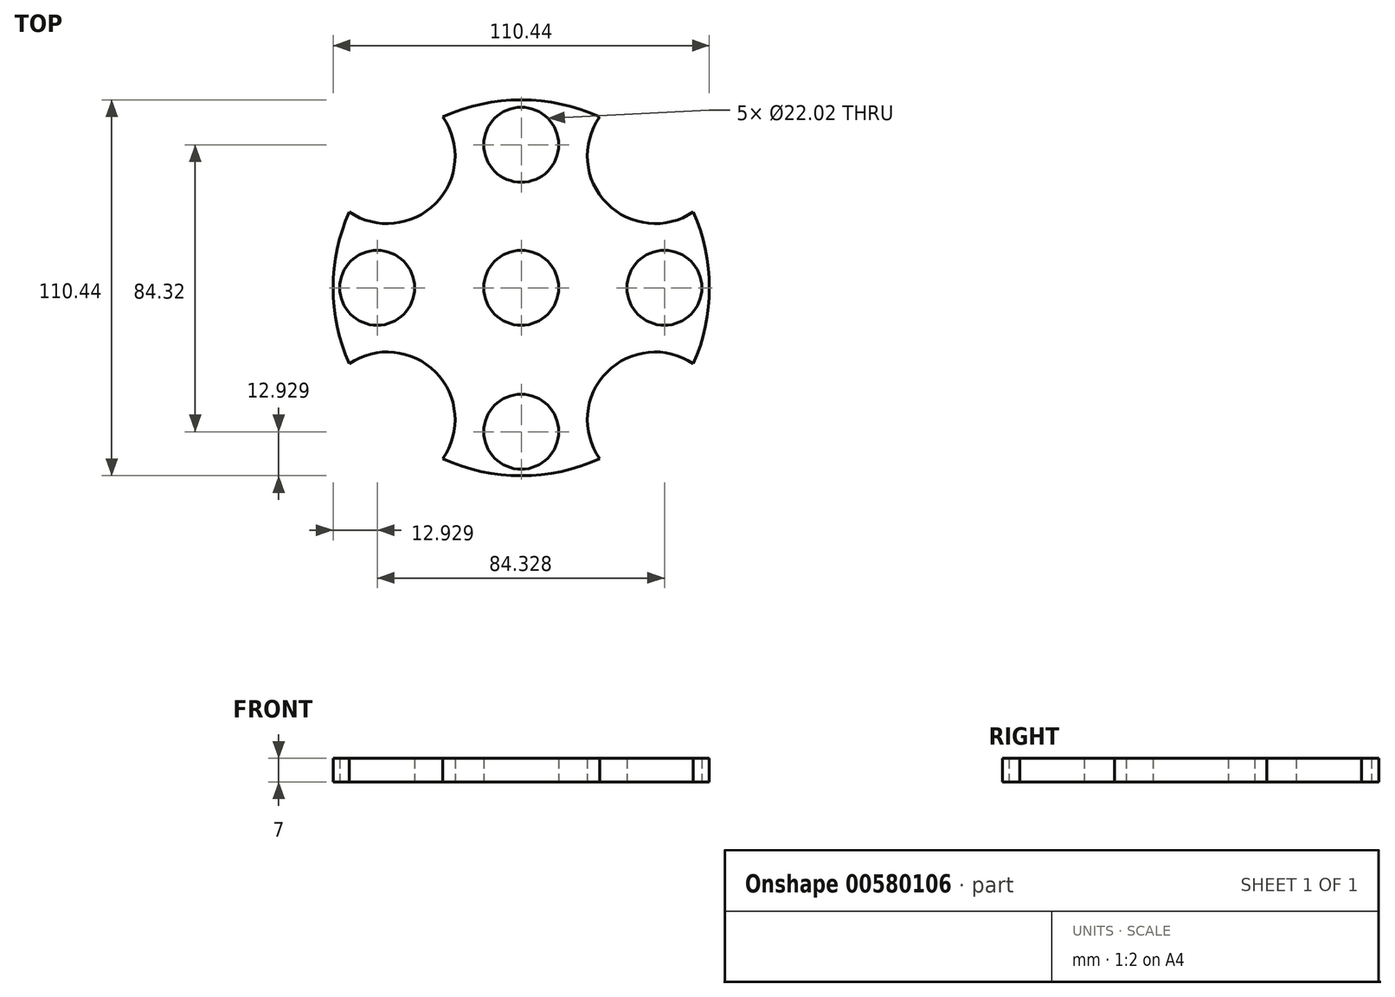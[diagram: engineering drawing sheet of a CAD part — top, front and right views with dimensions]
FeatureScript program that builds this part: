
annotation { "Feature Type Name" : "Feature", "Feature Type Description" : "" }
export const myFeature = defineFeature(function(context is Context, id is Id, definition is map)
    precondition{}
    {
        {
            var Q0;
            Q0=qCreatedBy(makeId("Top.planeOp"),FACE);
            var sketch = newSketch(context, id + "F0", { "sketchPlane" : qUnion([Q0])});
            skCircle(sketch, "E0", {"center": v(0, 0) * mm, "radius": 11.01 * mm});
            skCircle(sketch, "E1", {"center": v(0, 0) * mm, "radius": 55.22 * mm});
            skCircle(sketch, "E2", {"center": v(0, -42.3) * mm, "radius": 11.01 * mm});
            skCircle(sketch, "E3", {"center": v(42.04, 0) * mm, "radius": 11.01 * mm});
            skCircle(sketch, "E4", {"center": v(0, 42.03) * mm, "radius": 11.01 * mm});
            skCircle(sketch, "E5", {"center": v(-42.3, 0) * mm, "radius": 11.01 * mm});
            skCircle(sketch, "E6", {"center": v(39.33, -38.77) * mm, "radius": 19.92 * mm});
            skCircle(sketch, "E7", {"center": v(39.33, 38.77) * mm, "radius": 19.91 * mm});
            skCircle(sketch, "E8", {"center": v(-39.33, 38.77) * mm, "radius": 19.91 * mm});
            skCircle(sketch, "E9", {"center": v(-39.33, -38.77) * mm, "radius": 19.91 * mm});
            skSolve(sketch);
        }
        {
            var Q0;
            Q0=makeQuery(id+"F0.imprint","IMPRINT",FACE,{"disambiguationData":[TD([[makeQuery(id+"F0.imprint","IMPRINT",EDGE,{"derivedFrom":sQuery(id+"F0.wireOp",EDGE,"E0")}),-1.0]])]});
            extrude(context, id + "F1", {"entities" : qUnion([Q0]), "depth" : 7 * mm, "offsetDistance" : 25.4 * mm});
        }
    });
